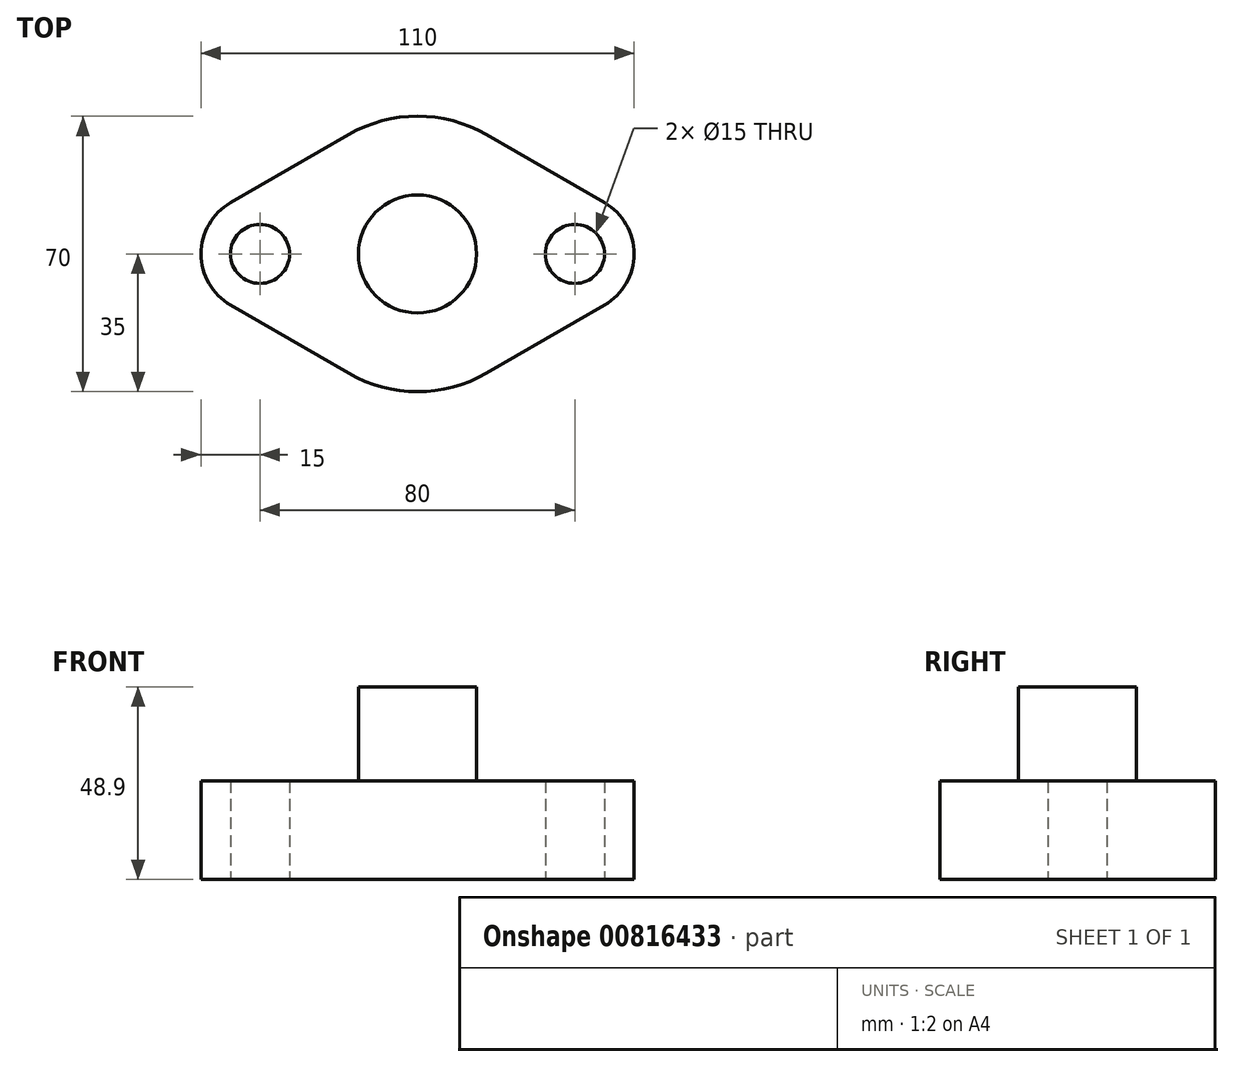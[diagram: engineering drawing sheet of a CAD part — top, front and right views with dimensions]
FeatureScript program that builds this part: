
annotation { "Feature Type Name" : "Feature", "Feature Type Description" : "" }
export const myFeature = defineFeature(function(context is Context, id is Id, definition is map)
    precondition{}
    {
        {
            var Q0;
            Q0=qCreatedBy(makeId("Top.planeOp"),FACE);
            var sketch = newSketch(context, id + "F0", { "sketchPlane" : qUnion([Q0])});
            skArc(sketch, "E0", {"start": v(-17.5, -30.31) * mm, "mid": v(0, -35) * mm, "end": v(17.5, -30.31) * mm});
            skArc(sketch, "E1", {"start": v(-47.5, 13) * mm, "mid": v(-55, 0) * mm, "end": v(-47.5, -13) * mm});
            skArc(sketch, "E2", {"start": v(47.5, -13) * mm, "mid": v(55, 0) * mm, "end": v(47.5, 13) * mm});
            skLineSegment(sketch, "E3", {"start": v(-47.5, 13) * mm, "end": v(-17.5, 30.31) * mm});
            skLineSegment(sketch, "E4", {"start": v(17.5, 30.31) * mm, "end": v(47.5, 13) * mm});
            skLineSegment(sketch, "E5", {"start": v(47.5, -13) * mm, "end": v(17.5, -30.31) * mm});
            skLineSegment(sketch, "E6", {"start": v(-17.5, -30.31) * mm, "end": v(-47.5, -13) * mm});
            skArc(sketch, "E7.trimOffspring", {"start": v(17.5, 30.31) * mm, "mid": v(0, 35) * mm, "end": v(-17.5, 30.31) * mm});
            skCircle(sketch, "E8", {"center": v(-40, 0) * mm, "radius": 7.5 * mm});
            skCircle(sketch, "E9", {"center": v(40, 0) * mm, "radius": 7.5 * mm});
            skSolve(sketch);
        }
        {
            var Q0;
            Q0=makeQuery(id+"F0.imprint","IMPRINT",FACE,{"disambiguationData":[TD([[makeQuery(id+"F0.imprint","IMPRINT",EDGE,{"derivedFrom":sQuery(id+"F0.wireOp",EDGE,"E0")}),1.0]])]});
            extrude(context, id + "F1", {"entities" : qUnion([Q0]), "depth" : 25 * mm, "offsetDistance" : 25 * mm});
        }
        {
            var Q0;
            Q0=makeQuery(id+"F1.opExtrude","CAP_FACE",FACE,{"disambiguationData":[OSD([sQuery(id+"F0.wireOp",EDGE,"E0"),sQuery(id+"F0.wireOp",EDGE,"E1"),sQuery(id+"F0.wireOp",EDGE,"E2"),sQuery(id+"F0.wireOp",EDGE,"E3"),sQuery(id+"F0.wireOp",EDGE,"E4"),sQuery(id+"F0.wireOp",EDGE,"E5"),sQuery(id+"F0.wireOp",EDGE,"E6"),sQuery(id+"F0.wireOp",EDGE,"E7.trimOffspring"),sQuery(id+"F0.wireOp",EDGE,"E8"),sQuery(id+"F0.wireOp",EDGE,"E9")])],"isStart":false});
            var sketch = newSketch(context, id + "F2", { "sketchPlane" : qUnion([Q0])});
            skCircle(sketch, "E10", {"center": v(0, 0) * mm, "radius": 15 * mm});
            skSolve(sketch);
        }
        {
            var Q0;
            Q0=makeQuery(id+"F2.imprint","IMPRINT",FACE,{"disambiguationData":[TD([[makeQuery(id+"F2.imprint","IMPRINT",EDGE,{"derivedFrom":sQuery(id+"F2.wireOp",EDGE,"E10")}),1.0]])]});
            var Q1;
            Q1=sQuery(id+"F2.wireOp",EDGE,"E10");
            extrude(context, id + "F3", {"entities" : qUnion([Q0]), "operationType" : NewBodyOperationType.ADD, "surfaceEntities" : qUnion([Q1]), "depth" : 23.9 * mm, "offsetDistance" : 25 * mm});
        }
    });
